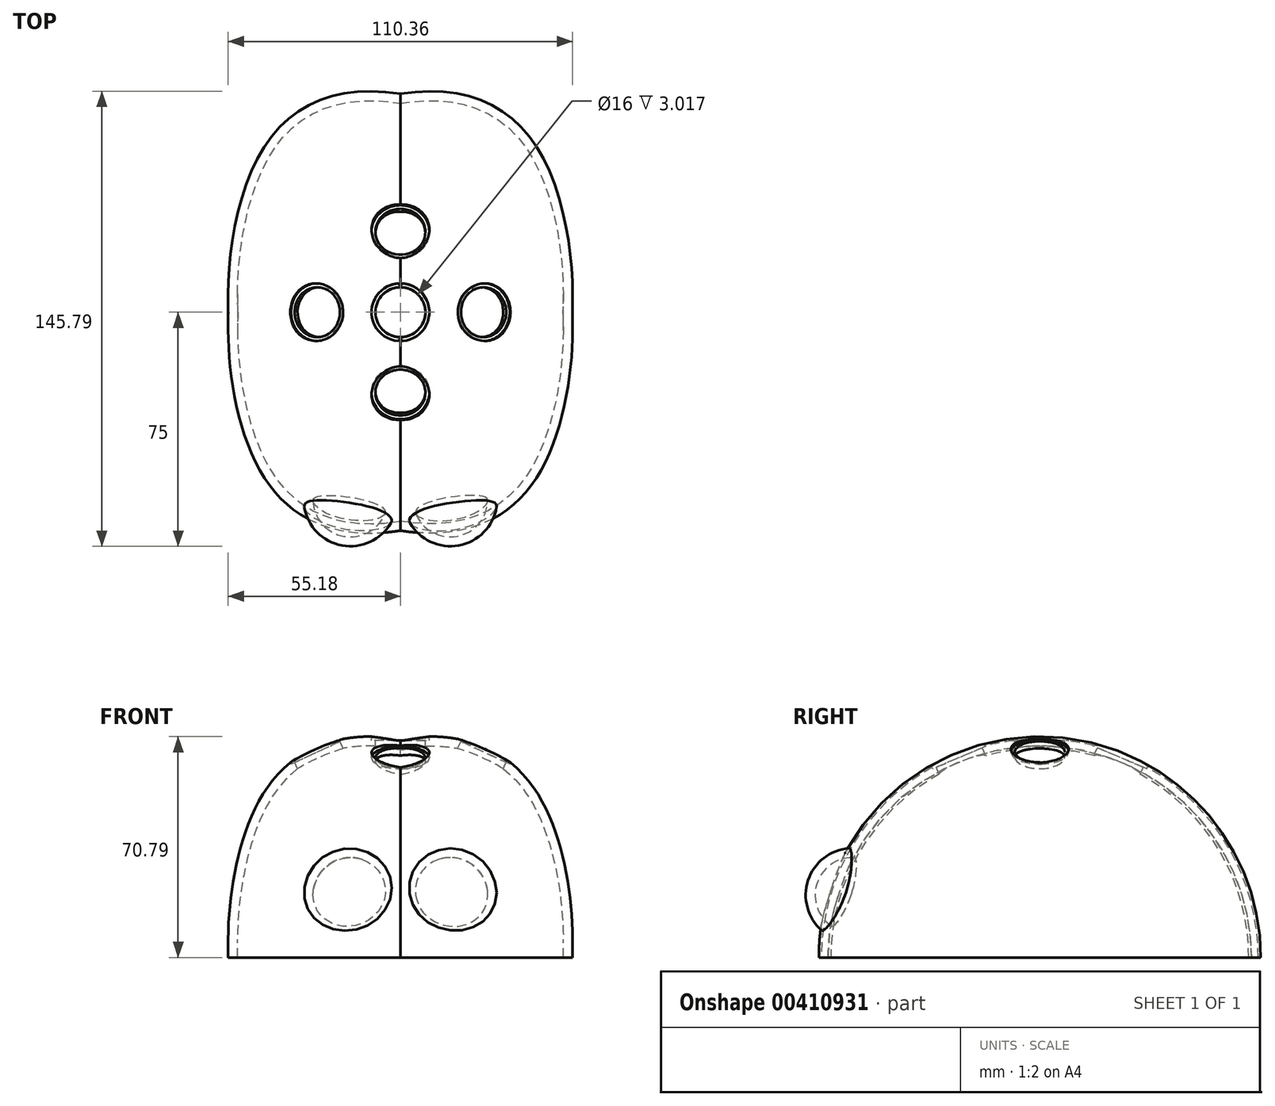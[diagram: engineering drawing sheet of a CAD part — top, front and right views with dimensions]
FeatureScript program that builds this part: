
annotation { "Feature Type Name" : "Feature", "Feature Type Description" : "" }
export const myFeature = defineFeature(function(context is Context, id is Id, definition is map)
    precondition{}
    {
        {
            var Q0;
            Q0=qCreatedBy(makeId("Top.planeOp"),FACE);
            var sketch = newSketch(context, id + "F0", { "sketchPlane" : qUnion([Q0])});
            skPoint(sketch, "E0.0.internal.orphan", {"position": v(-55, 0) * mm});
            skPoint(sketch, "E0.3.internal.orphan", {"position": v(0, 70) * mm});
            skFitSpline(sketch, "E1", {"points": [v(-55, 0) * mm, v(-43, 54) * mm, v(0, 70) * mm], "startDerivative": vector(-5.73, 85.98) * mm, "endDerivative": vector(119.59, -18.88) * mm});
            skFitSpline(sketch, "E2.MirrorCS", {"points": [v(55, 0) * mm, v(43, 54) * mm, v(0, 70) * mm], "startDerivative": vector(5.73, 85.98) * mm, "endDerivative": vector(-119.59, -18.88) * mm});
            skLineSegment(sketch, "E3", {"start": v(-55, 0) * mm, "end": v(55, 0) * mm});
            skSolve(sketch);
        }
        {
            var Q0;
            Q0=makeQuery(id+"F0.imprint","IMPRINT",FACE,{"disambiguationData":[TD([[makeQuery(id+"F0.imprint","IMPRINT",EDGE,{"derivedFrom":sQuery(id+"F0.wireOp",EDGE,"E1")}),-1.0]])]});
            var Q1;
            Q1=sQuery(id+"F0.wireOp",EDGE,"E3");
            revolve(context, id + "F1", {"entities" : qUnion([Q0]), "axis" : qUnion([Q1]), "revolveType" : RevolveType.ONE_DIRECTION, "angle" : 180 * degree});
        }
        {
            var Q0;
            Q0=qCreatedBy(makeId("Front.planeOp"),FACE);
            cPlane(context, id + "F2", {"entities" : qUnion([Q0]), "cplaneType" : CPlaneType.OFFSET, "offset" : 60 * mm, "width" : 150 * mm, "height" : 150 * mm});
        }
        {
            var Q0;
            Q0=qCreatedBy(id+"F2.planeOp",FACE);
            var sketch = newSketch(context, id + "F3", { "sketchPlane" : qUnion([Q0])});
            skArc(sketch, "E4", {"start": v(-16, 35) * mm, "mid": v(-31, 20) * mm, "end": v(-16, 5) * mm});
            skLineSegment(sketch, "E5", {"start": v(-16, 35) * mm, "end": v(-16, 5) * mm});
            skSolve(sketch);
        }
        {
            var Q0;
            Q0 = qSketchRegion(id + "F3", true);
            var Q1;
            Q1=sQuery(id+"F3.wireOp",EDGE,"E5");
            revolve(context, id + "F4", {"operationType" : NewBodyOperationType.ADD, "entities" : qUnion([Q0]), "axis" : qUnion([Q1]), "revolveType" : RevolveType.FULL, "oppositeDirection" : true});
        }
        {
            var Q0;
            Q0=qCreatedBy(id+"F2.planeOp",FACE);
            var sketch = newSketch(context, id + "F5", { "sketchPlane" : qUnion([Q0])});
            skArc(sketch, "E6", {"start": v(16, 5) * mm, "mid": v(31, 20) * mm, "end": v(16, 35) * mm});
            skLineSegment(sketch, "E7", {"start": v(16, 35) * mm, "end": v(16, 5) * mm});
            skSolve(sketch);
        }
        {
            var Q0;
            Q0 = qSketchRegion(id + "F5", true);
            var Q1;
            Q1=sQuery(id+"F5.wireOp",EDGE,"E7");
            revolve(context, id + "F6", {"operationType" : NewBodyOperationType.ADD, "entities" : qUnion([Q0]), "axis" : qUnion([Q1]), "revolveType" : RevolveType.FULL});
        }
        {
            var Q0;
            Q0=makeQuery(id+"F1.opRevolve","CAP_FACE",FACE,{"disambiguationData":[OSD([sQuery(id+"F0.wireOp",EDGE,"E1"),sQuery(id+"F0.wireOp",EDGE,"E2.MirrorCS"),sQuery(id+"F0.wireOp",EDGE,"E3")])],"isStart":false});
            shell(context, id + "F7", {"entities" : qUnion([Q0]), "thickness" : 3 * mm});
        }
        {
            var Q0;
            Q0=qCreatedBy(makeId("Top.planeOp"),FACE);
            cPlane(context, id + "F8", {"entities" : qUnion([Q0]), "cplaneType" : CPlaneType.OFFSET, "offset" : 75 * mm, "width" : 150 * mm, "height" : 150 * mm});
        }
        {
            var Q0;
            Q0=qCreatedBy(id+"F8.planeOp",FACE);
            var sketch = newSketch(context, id + "F9", { "sketchPlane" : qUnion([Q0])});
            skCircle(sketch, "E8", {"center": v(0, 0) * mm, "radius": 8 * mm});
            skSolve(sketch);
        }
        {
            var Q0;
            Q0 = qSketchRegion(id + "F9", true);
            extrude(context, id + "F10", {"entities" : qUnion([Q0]), "operationType" : NewBodyOperationType.REMOVE, "endBound" : BoundingType.THROUGH_ALL, "oppositeDirection" : true, "depth" : 25 * mm});
        }
        {
            var Q0;
            Q0=qCreatedBy(id+"F8.planeOp",FACE);
            var sketch = newSketch(context, id + "F11", { "sketchPlane" : qUnion([Q0])});
            skCircle(sketch, "E9", {"center": v(0, 0) * mm, "radius": 9.25 * mm});
            skSolve(sketch);
        }
        {
            var Q0;
            Q0 = qSketchRegion(id + "F11", true);
            extrude(context, id + "F12", {"entities" : qUnion([Q0]), "operationType" : NewBodyOperationType.REMOVE, "oppositeDirection" : true, "depth" : 5.5 * mm});
        }
        {
            var Q0;
            Q0=qCreatedBy(id+"F8.planeOp",FACE);
            var sketch = newSketch(context, id + "F13", { "sketchPlane" : qUnion([Q0])});
            skLineSegment(sketch, "E10", {"start": v(55.23, 0) * mm, "end": v(-55.23, 0) * mm, "construction": true});
            skLineSegment(sketch, "E11", {"start": v(0, 47.32) * mm, "end": v(0, -38.58) * mm, "construction": true});
            skSolve(sketch);
        }
        {
            var Q0;
            Q0=qCreatedBy(id+"F8.planeOp",FACE);
            var Q1;
            Q1=sQuery(id+"F13.wireOp",EDGE,"E10");
            cPlane(context, id + "F14", {"entities" : qUnion([Q0, Q1]), "cplaneType" : CPlaneType.LINE_ANGLE, "offset" : 25 * mm, "angle" : 23 * degree, "width" : 150 * mm, "height" : 150 * mm});
        }
        {
            var Q0;
            Q0=qCreatedBy(id+"F14.planeOp",FACE);
            cPlane(context, id + "F15", {"entities" : qUnion([Q0]), "cplaneType" : CPlaneType.OFFSET, "offset" : 5 * mm, "oppositeDirection" : true, "width" : 150 * mm, "height" : 150 * mm});
        }
        {
            var Q0;
            Q0=qCreatedBy(id+"F15.planeOp",FACE);
            var sketch = newSketch(context, id + "F16", { "sketchPlane" : qUnion([Q0])});
            skCircle(sketch, "E12", {"center": v(0, 1.3) * mm, "radius": 8 * mm});
            skSolve(sketch);
        }
        {
            var Q0;
            Q0 = qSketchRegion(id + "F16", true);
            extrude(context, id + "F17", {"entities" : qUnion([Q0]), "operationType" : NewBodyOperationType.REMOVE, "endBound" : BoundingType.THROUGH_ALL, "depth" : 25 * mm});
        }
        {
            var Q0;
            Q0=qCreatedBy(id+"F15.planeOp",FACE);
            var sketch = newSketch(context, id + "F18", { "sketchPlane" : qUnion([Q0])});
            skCircle(sketch, "E13", {"center": v(0, 1.3) * mm, "radius": 9.25 * mm});
            skSolve(sketch);
        }
        {
            var Q0;
            Q0 = qSketchRegion(id + "F18", true);
            extrude(context, id + "F19", {"entities" : qUnion([Q0]), "operationType" : NewBodyOperationType.REMOVE, "depth" : 5 * mm});
        }
        {
            var Q0;
            Q0=qCreatedBy(id+"F8.planeOp",FACE);
            var Q1;
            Q1=sQuery(id+"F13.wireOp",EDGE,"E10");
            cPlane(context, id + "F20", {"entities" : qUnion([Q0, Q1]), "cplaneType" : CPlaneType.LINE_ANGLE, "offset" : 25 * mm, "angle" : 23 * degree, "oppositeDirection" : true, "width" : 150 * mm, "height" : 150 * mm});
        }
        {
            var Q0;
            Q0=qCreatedBy(id+"F20.planeOp",FACE);
            cPlane(context, id + "F21", {"entities" : qUnion([Q0]), "cplaneType" : CPlaneType.OFFSET, "offset" : 5 * mm, "oppositeDirection" : true, "width" : 150 * mm, "height" : 150 * mm});
        }
        {
            var Q0;
            Q0=qCreatedBy(id+"F21.planeOp",FACE);
            var sketch = newSketch(context, id + "F22", { "sketchPlane" : qUnion([Q0])});
            skCircle(sketch, "E14", {"center": v(0, -1.3) * mm, "radius": 8 * mm});
            skSolve(sketch);
        }
        {
            var Q0;
            Q0 = qSketchRegion(id + "F22", true);
            extrude(context, id + "F23", {"entities" : qUnion([Q0]), "operationType" : NewBodyOperationType.REMOVE, "endBound" : BoundingType.THROUGH_ALL, "depth" : 25 * mm});
        }
        {
            var Q0;
            Q0=qCreatedBy(id+"F21.planeOp",FACE);
            var sketch = newSketch(context, id + "F24", { "sketchPlane" : qUnion([Q0])});
            skCircle(sketch, "E15", {"center": v(0, -1.3) * mm, "radius": 9.25 * mm});
            skSolve(sketch);
        }
        {
            var Q0;
            Q0 = qSketchRegion(id + "F24", true);
            extrude(context, id + "F25", {"entities" : qUnion([Q0]), "operationType" : NewBodyOperationType.REMOVE, "depth" : 5 * mm});
        }
        {
            var Q0;
            Q0=qCreatedBy(id+"F8.planeOp",FACE);
            var Q1;
            Q1=sQuery(id+"F13.wireOp",EDGE,"E11");
            cPlane(context, id + "F26", {"entities" : qUnion([Q0, Q1]), "cplaneType" : CPlaneType.LINE_ANGLE, "offset" : 25 * mm, "angle" : 25 * degree, "width" : 150 * mm, "height" : 150 * mm});
        }
        {
            var Q0;
            Q0=qCreatedBy(id+"F26.planeOp",FACE);
            cPlane(context, id + "F27", {"entities" : qUnion([Q0]), "cplaneType" : CPlaneType.OFFSET, "offset" : 8 * mm, "oppositeDirection" : true, "width" : 150 * mm, "height" : 150 * mm});
        }
        {
            var Q0;
            Q0=qCreatedBy(id+"F27.planeOp",FACE);
            var sketch = newSketch(context, id + "F28", { "sketchPlane" : qUnion([Q0])});
            skCircle(sketch, "E16", {"center": v(3.7, 0) * mm, "radius": 8 * mm});
            skSolve(sketch);
        }
        {
            var Q0;
            Q0 = qSketchRegion(id + "F28", true);
            extrude(context, id + "F29", {"entities" : qUnion([Q0]), "operationType" : NewBodyOperationType.REMOVE, "endBound" : BoundingType.THROUGH_ALL, "depth" : 25 * mm});
        }
        {
            var Q0;
            Q0=qCreatedBy(id+"F27.planeOp",FACE);
            var sketch = newSketch(context, id + "F30", { "sketchPlane" : qUnion([Q0])});
            skCircle(sketch, "E17", {"center": v(3.7, 0) * mm, "radius": 9.25 * mm});
            skSolve(sketch);
        }
        {
            var Q0;
            Q0 = qSketchRegion(id + "F30", true);
            extrude(context, id + "F31", {"entities" : qUnion([Q0]), "operationType" : NewBodyOperationType.REMOVE, "depth" : 5 * mm});
        }
        {
            var Q0;
            Q0=qCreatedBy(id+"F8.planeOp",FACE);
            var Q1;
            Q1=sQuery(id+"F13.wireOp",EDGE,"E11");
            cPlane(context, id + "F32", {"entities" : qUnion([Q0, Q1]), "cplaneType" : CPlaneType.LINE_ANGLE, "offset" : 25 * mm, "angle" : 25 * degree, "oppositeDirection" : true, "width" : 150 * mm, "height" : 150 * mm});
        }
        {
            var Q0;
            Q0=qCreatedBy(id+"F32.planeOp",FACE);
            cPlane(context, id + "F33", {"entities" : qUnion([Q0]), "cplaneType" : CPlaneType.OFFSET, "offset" : 8 * mm, "oppositeDirection" : true, "width" : 150 * mm, "height" : 150 * mm});
        }
        {
            var Q0;
            Q0=qCreatedBy(id+"F33.planeOp",FACE);
            var sketch = newSketch(context, id + "F34", { "sketchPlane" : qUnion([Q0])});
            skCircle(sketch, "E18", {"center": v(-3.7, 0) * mm, "radius": 8 * mm});
            skSolve(sketch);
        }
        {
            var Q0;
            Q0 = qSketchRegion(id + "F34", true);
            extrude(context, id + "F35", {"entities" : qUnion([Q0]), "operationType" : NewBodyOperationType.REMOVE, "endBound" : BoundingType.THROUGH_ALL, "depth" : 25 * mm});
        }
        {
            var Q0;
            Q0=qCreatedBy(id+"F33.planeOp",FACE);
            var sketch = newSketch(context, id + "F36", { "sketchPlane" : qUnion([Q0])});
            skCircle(sketch, "E19", {"center": v(-3.7, 0) * mm, "radius": 9.25 * mm});
            skSolve(sketch);
        }
        {
            var Q0;
            Q0 = qSketchRegion(id + "F36", true);
            extrude(context, id + "F37", {"entities" : qUnion([Q0]), "operationType" : NewBodyOperationType.REMOVE, "depth" : 5 * mm});
        }
    });
